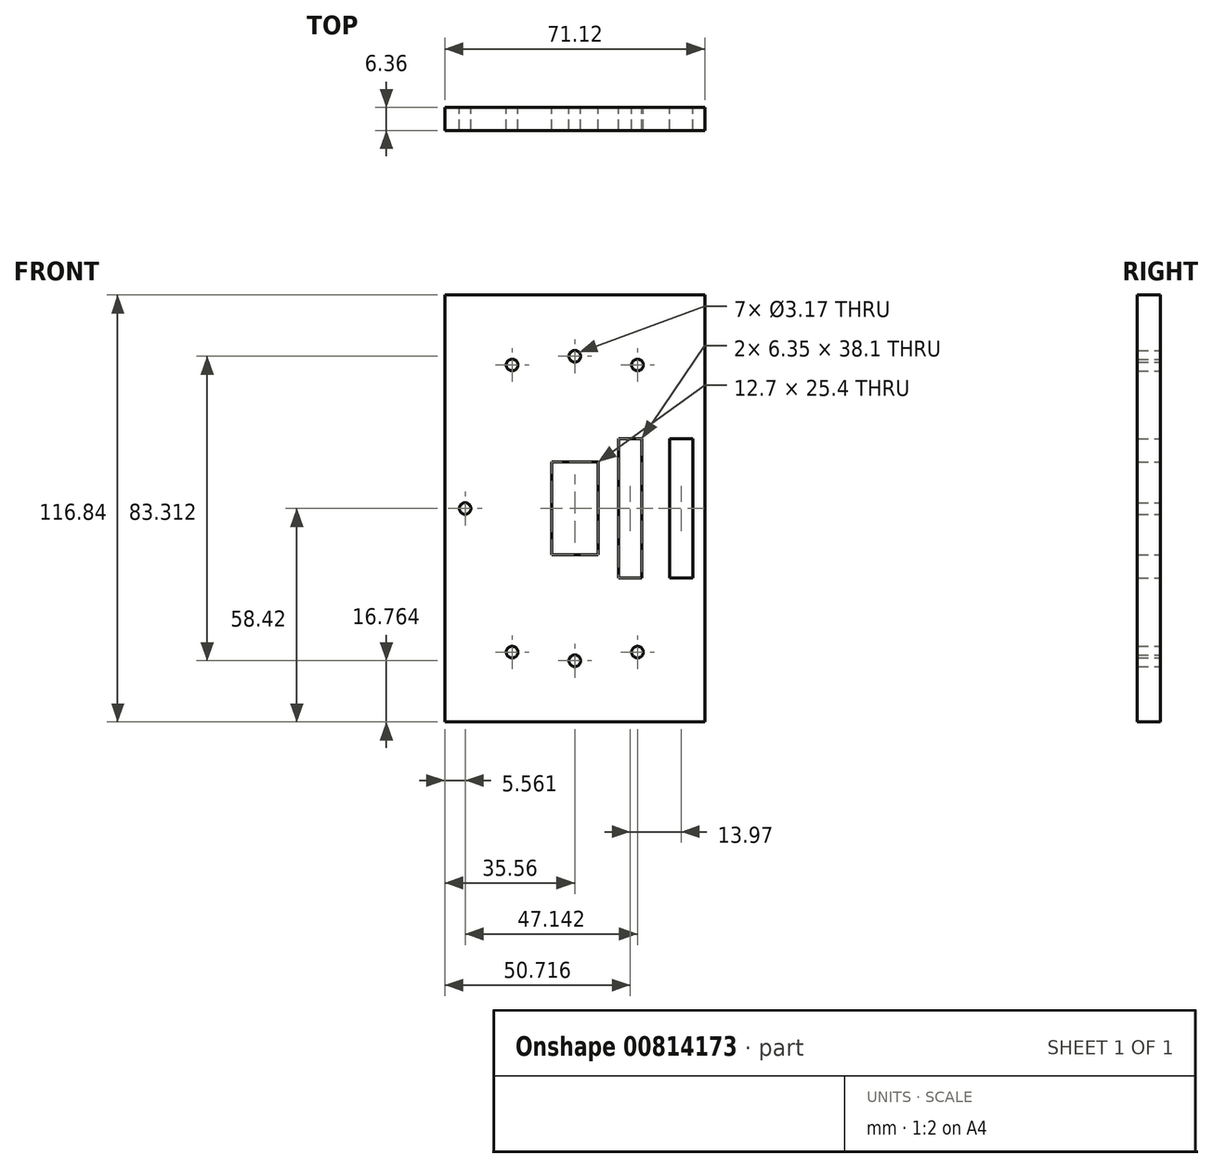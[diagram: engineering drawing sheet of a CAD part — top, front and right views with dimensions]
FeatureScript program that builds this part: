
annotation { "Feature Type Name" : "Feature", "Feature Type Description" : "" }
export const myFeature = defineFeature(function(context is Context, id is Id, definition is map)
    precondition{}
    {
        {
            var Q0;
            Q0=qCreatedBy(makeId("Front.planeOp"),FACE);
            var sketch = newSketch(context, id + "F0", { "sketchPlane" : qUnion([Q0])});
            skLineSegment(sketch, "E0.bottom", {"start": v(35.56, 58.42) * mm, "end": v(-35.56, 58.42) * mm});
            skLineSegment(sketch, "E0.top", {"start": v(35.56, -58.42) * mm, "end": v(-35.56, -58.42) * mm});
            skLineSegment(sketch, "E0.left", {"start": v(35.56, 58.42) * mm, "end": v(35.56, -58.42) * mm});
            skLineSegment(sketch, "E0.right", {"start": v(-35.56, 58.42) * mm, "end": v(-35.56, -58.42) * mm});
            skPoint(sketch, "E0.middle", {"position": v(0, 0) * mm});
            skLineSegment(sketch, "E1.bottom", {"start": v(-6.35, 12.7) * mm, "end": v(6.35, 12.7) * mm});
            skLineSegment(sketch, "E1.top", {"start": v(-6.35, -12.7) * mm, "end": v(6.35, -12.7) * mm});
            skLineSegment(sketch, "E1.left", {"start": v(-6.35, 12.7) * mm, "end": v(-6.35, -12.7) * mm});
            skCircle(sketch, "E2", {"center": v(-17.14, 39.29) * mm, "radius": 1.59 * mm});
            skCircle(sketch, "E3.MirrorC", {"center": v(17.14, 39.29) * mm, "radius": 1.59 * mm});
            skCircle(sketch, "E4.MirrorC", {"center": v(-17.14, -39.29) * mm, "radius": 1.59 * mm});
            skCircle(sketch, "E5.MirrorC", {"center": v(17.14, -39.29) * mm, "radius": 1.59 * mm});
            skLineSegment(sketch, "E6", {"start": v(-15.85, 0) * mm, "end": v(-101.5, 0) * mm});
            skPoint(sketch, "E6.startSnap0", {"position": v(-6.35, 0) * mm});
            skLineSegment(sketch, "E7", {"start": v(6.35, 12.7) * mm, "end": v(6.35, -12.7) * mm});
            skPoint(sketch, "E8.middle", {"position": v(9.99, 0) * mm});
            skLineSegment(sketch, "E9", {"start": v(0, 12.7) * mm, "end": v(0, 41.66) * mm});
            skCircle(sketch, "E10", {"center": v(0, 41.66) * mm, "radius": 1.59 * mm});
            skCircle(sketch, "E11.MirrorC", {"center": v(0, -41.66) * mm, "radius": 1.59 * mm});
            skLineSegment(sketch, "E12.bottom", {"start": v(32.3, 19.05) * mm, "end": v(25.95, 19.05) * mm});
            skLineSegment(sketch, "E12.top", {"start": v(32.3, -19.05) * mm, "end": v(25.95, -19.05) * mm});
            skLineSegment(sketch, "E12.left", {"start": v(32.3, 19.05) * mm, "end": v(32.3, -19.05) * mm});
            skLineSegment(sketch, "E12.right", {"start": v(25.95, 19.05) * mm, "end": v(25.95, -19.05) * mm});
            skPoint(sketch, "E12.middle", {"position": v(29.13, 0) * mm});
            skLineSegment(sketch, "E13", {"start": v(22.14, 0) * mm, "end": v(22.14, 29.1) * mm});
            skLineSegment(sketch, "E14.MirrorCS", {"start": v(18.33, 19.05) * mm, "end": v(18.33, -19.05) * mm});
            skLineSegment(sketch, "E15.MirrorCS", {"start": v(11.98, 19.05) * mm, "end": v(18.33, 19.05) * mm});
            skLineSegment(sketch, "E16.MirrorCS", {"start": v(11.98, 19.05) * mm, "end": v(11.98, -19.05) * mm});
            skLineSegment(sketch, "E17.MirrorCS", {"start": v(11.98, -19.05) * mm, "end": v(18.33, -19.05) * mm});
            skCircle(sketch, "E18", {"center": v(-30, 0) * mm, "radius": 1.59 * mm});
            skSolve(sketch);
        }
        {
            var Q0;
            Q0=makeQuery(id+"F0.imprint","IMPRINT",FACE,{"disambiguationData":[TD([[makeQuery(id+"F0.imprint","IMPRINT",EDGE,{"derivedFrom":sQuery(id+"F0.wireOp",EDGE,"E0.bottom")}),1.0]])]});
            var Q1;
            {var subQ0=sQuery(id+"F0.wireOp",EDGE,"02456610-d92d-464a-957a-78d5448d8da0.0");Q1=makeQuery(id+"F0.imprint","IMPRINT",FACE,{"disambiguationData":[TD([[makeQuery(id+"F0.imprint","IMPRINT",EDGE,{"derivedFrom":subQ0}),-1.0]])]});}
            extrude(context, id + "F1", {"entities" : qUnion([Q0, Q1]), "endBound" : BoundingType.SYMMETRIC, "depth" : 6.35 * mm, "offsetDistance" : 25 * mm});
        }
        {
            var Q0;
            Q0=makeQuery(id+"F0.imprint","IMPRINT",FACE,{"disambiguationData":[TD([[makeQuery(id+"F0.imprint","IMPRINT",EDGE,{"derivedFrom":sQuery(id+"F0.wireOp",EDGE,"E14.MirrorCS")}),-1.0]])]});
            var Q1;
            Q1=makeQuery(id+"F0.imprint","IMPRINT",FACE,{"disambiguationData":[TD([[makeQuery(id+"F0.imprint","IMPRINT",EDGE,{"derivedFrom":sQuery(id+"F0.wireOp",EDGE,"E12.bottom")}),1.0]])]});
            extrude(context, id + "F2", {"entities" : qUnion([Q0, Q1]), "operationType" : NewBodyOperationType.REMOVE, "oppositeDirection" : true, "depth" : 2.54 * mm, "offsetDistance" : 25.4 * mm});
        }
    });
